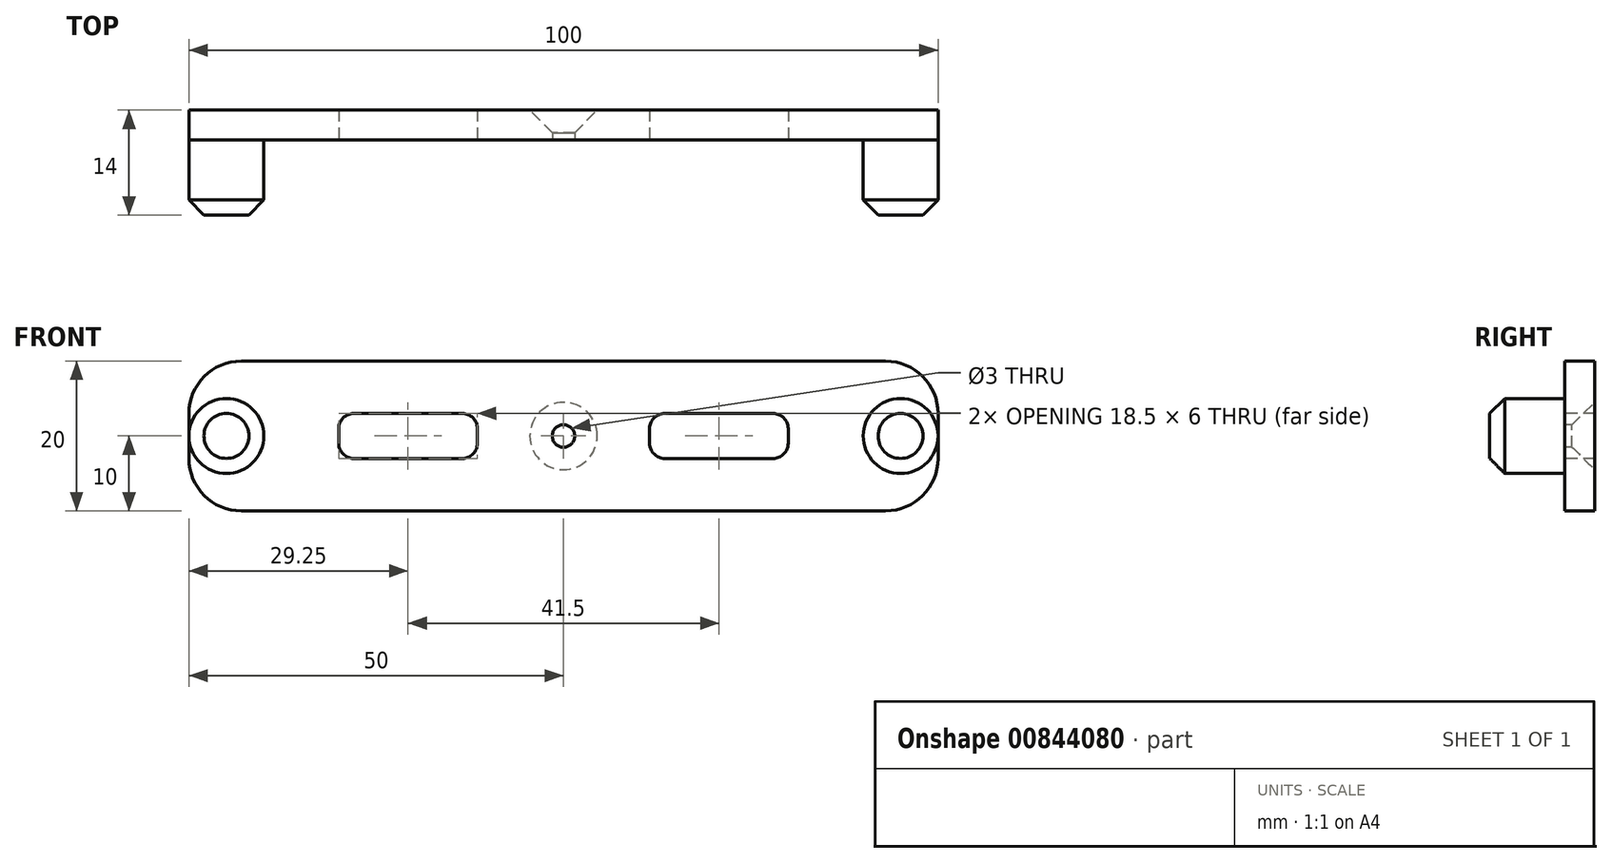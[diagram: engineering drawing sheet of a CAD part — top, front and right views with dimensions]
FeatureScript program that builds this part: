
annotation { "Feature Type Name" : "Feature", "Feature Type Description" : "" }
export const myFeature = defineFeature(function(context is Context, id is Id, definition is map)
    precondition{}
    {
        {
            var Q0;
            Q0=qCreatedBy(makeId("Front.planeOp"),FACE);
            var sketch = newSketch(context, id + "F0", { "sketchPlane" : qUnion([Q0])});
            skLineSegment(sketch, "E0.bottom", {"start": v(-50, 10) * mm, "end": v(50, 10) * mm});
            skLineSegment(sketch, "E0.top", {"start": v(-50, -10) * mm, "end": v(50, -10) * mm});
            skLineSegment(sketch, "E0.left", {"start": v(-50, 10) * mm, "end": v(-50, -10) * mm});
            skLineSegment(sketch, "E0.right", {"start": v(50, 10) * mm, "end": v(50, -10) * mm});
            skPoint(sketch, "E0.middle", {"position": v(0, 0) * mm});
            skSolve(sketch);
        }
        {
            var Q0;
            Q0=makeQuery(id+"F0.imprint","IMPRINT",FACE,{"disambiguationData":[TD([[makeQuery(id+"F0.imprint","IMPRINT",EDGE,{"derivedFrom":sQuery(id+"F0.wireOp",EDGE,"E0.bottom")}),-1.0]])]});
            extrude(context, id + "F1", {"entities" : qUnion([Q0]), "depth" : 4 * mm, "offsetDistance" : 25 * mm});
        }
        {
            var Q0;
            Q0=makeQuery(id+"F1.opExtrude","CAP_FACE",FACE,{"disambiguationData":[OSD([sQuery(id+"F0.wireOp",EDGE,"E0.bottom"),sQuery(id+"F0.wireOp",EDGE,"E0.top"),sQuery(id+"F0.wireOp",EDGE,"E0.left"),sQuery(id+"F0.wireOp",EDGE,"E0.right")])],"isStart":false});
            var sketch = newSketch(context, id + "F2", { "sketchPlane" : qUnion([Q0])});
            skCircle(sketch, "E1", {"center": v(-45, 0) * mm, "radius": 5 * mm});
            skPoint(sketch, "E1.centerSnap0", {"position": v(-50, 0) * mm});
            skCircle(sketch, "E2", {"center": v(45, 0) * mm, "radius": 5 * mm});
            skSolve(sketch);
        }
        {
            var Q0;
            Q0=makeQuery(id+"F2.imprint","IMPRINT",FACE,{"disambiguationData":[TD([[makeQuery(id+"F2.imprint","IMPRINT",EDGE,{"derivedFrom":sQuery(id+"F2.wireOp",EDGE,"E1")}),1.0]])]});
            var Q1;
            Q1=makeQuery(id+"F2.imprint","IMPRINT",FACE,{"disambiguationData":[TD([[makeQuery(id+"F2.imprint","IMPRINT",EDGE,{"derivedFrom":sQuery(id+"F2.wireOp",EDGE,"E2")}),1.0]])]});
            extrude(context, id + "F3", {"entities" : qUnion([Q0, Q1]), "operationType" : NewBodyOperationType.ADD, "depth" : 10 * mm, "offsetDistance" : 25 * mm});
        }
        {
            var Q0;
            Q0=makeQuery(id+"F1.opExtrude","SWEPT_EDGE",EDGE,{"disambiguationData":[OSD([sQuery(id+"F0.wireOp",EDGE,"E0.top"),sQuery(id+"F0.wireOp",EDGE,"E0.left")])]});
            var Q1;
            Q1=makeQuery(id+"F1.opExtrude","SWEPT_EDGE",EDGE,{"disambiguationData":[OSD([sQuery(id+"F0.wireOp",EDGE,"E0.top"),sQuery(id+"F0.wireOp",EDGE,"E0.right")])]});
            var Q2;
            Q2=makeQuery(id+"F1.opExtrude","SWEPT_EDGE",EDGE,{"disambiguationData":[OSD([sQuery(id+"F0.wireOp",EDGE,"E0.bottom"),sQuery(id+"F0.wireOp",EDGE,"E0.right")])]});
            var Q3;
            Q3=makeQuery(id+"F1.opExtrude","SWEPT_EDGE",EDGE,{"disambiguationData":[OSD([sQuery(id+"F0.wireOp",EDGE,"E0.bottom"),sQuery(id+"F0.wireOp",EDGE,"E0.left")])]});
            fillet(context, id + "F4", {"entities" : qUnion([Q0, Q1, Q2, Q3]), "radius" : 7 * mm, "tangentPropagation" : true, "allowEdgeOverflow" : false});
        }
        {
            var Q0;
            Q0=makeQuery(id+"F1.opExtrude","CAP_FACE",FACE,{"disambiguationData":[OSD([sQuery(id+"F0.wireOp",EDGE,"E0.bottom"),sQuery(id+"F0.wireOp",EDGE,"E0.top"),sQuery(id+"F0.wireOp",EDGE,"E0.left"),sQuery(id+"F0.wireOp",EDGE,"E0.right")])],"isStart":false});
            var sketch = newSketch(context, id + "F5", { "sketchPlane" : qUnion([Q0])});
            skCircle(sketch, "E3", {"center": v(0, 0) * mm, "radius": 1.5 * mm});
            skSolve(sketch);
        }
        {
            var Q0;
            Q0 = qSketchRegion(id + "F5", true);
            extrude(context, id + "F6", {"entities" : qUnion([Q0]), "operationType" : NewBodyOperationType.REMOVE, "oppositeDirection" : true, "depth" : 25 * mm, "offsetDistance" : 25 * mm});
        }
        {
            var Q0;
            Q0=makeQuery(id+"F6.boolean.opBoolean","INTERSECT",EDGE,{"derivedFrom":[makeQuery(id+"F1.opExtrude","CAP_FACE",FACE,{"disambiguationData":[OSD([sQuery(id+"F0.wireOp",EDGE,"E0.bottom"),sQuery(id+"F0.wireOp",EDGE,"E0.top"),sQuery(id+"F0.wireOp",EDGE,"E0.left"),sQuery(id+"F0.wireOp",EDGE,"E0.right")])],"isStart":true}),makeQuery(id+"F6.opExtrude","SWEPT_FACE",FACE,{"disambiguationData":[OSD([sQuery(id+"F5.wireOp",EDGE,"E3")])]})]});
            chamfer(context, id + "F7", {"entities" : qUnion([Q0]), "width" : 3 * mm, "tangentPropagation" : true});
        }
        {
            var Q0;
            Q0=makeQuery(id+"F1.opExtrude","CAP_FACE",FACE,{"disambiguationData":[OSD([sQuery(id+"F0.wireOp",EDGE,"E0.bottom"),sQuery(id+"F0.wireOp",EDGE,"E0.top"),sQuery(id+"F0.wireOp",EDGE,"E0.left"),sQuery(id+"F0.wireOp",EDGE,"E0.right")])],"isStart":false});
            var sketch = newSketch(context, id + "F8", { "sketchPlane" : qUnion([Q0])});
            skLineSegment(sketch, "E4.bottom", {"start": v(-30, 3) * mm, "end": v(-11.5, 3) * mm});
            skLineSegment(sketch, "E4.top", {"start": v(-30, -3) * mm, "end": v(-11.5, -3) * mm});
            skLineSegment(sketch, "E4.left", {"start": v(-30, 3) * mm, "end": v(-30, -3) * mm});
            skLineSegment(sketch, "E4.right", {"start": v(-11.5, 3) * mm, "end": v(-11.5, -3) * mm});
            skLineSegment(sketch, "E5", {"start": v(0, 0) * mm, "end": v(0, 30.26) * mm, "construction": true});
            skLineSegment(sketch, "E6.MirrorCS", {"start": v(30, 3) * mm, "end": v(11.5, 3) * mm});
            skLineSegment(sketch, "E7.MirrorCS", {"start": v(11.5, 3) * mm, "end": v(11.5, -3) * mm});
            skLineSegment(sketch, "E8.MirrorCS", {"start": v(30, 3) * mm, "end": v(30, -3) * mm});
            skLineSegment(sketch, "E9.MirrorCS", {"start": v(30, -3) * mm, "end": v(11.5, -3) * mm});
            skSolve(sketch);
        }
        {
            var Q0;
            Q0 = qSketchRegion(id + "F8", true);
            extrude(context, id + "F9", {"entities" : qUnion([Q0]), "operationType" : NewBodyOperationType.REMOVE, "oppositeDirection" : true, "depth" : 25 * mm, "offsetDistance" : 25 * mm});
        }
        {
            var Q0;
            Q0=makeQuery(id+"F9.boolean.opBoolean","COPY",EDGE,{"derivedFrom":makeQuery(id+"F9.opExtrude","SWEPT_EDGE",EDGE,{"disambiguationData":[OSD([sQuery(id+"F8.wireOp",EDGE,"E4.bottom"),sQuery(id+"F8.wireOp",EDGE,"E4.left")])]})});
            var Q1;
            Q1=makeQuery(id+"F9.boolean.opBoolean","COPY",EDGE,{"derivedFrom":makeQuery(id+"F9.opExtrude","SWEPT_EDGE",EDGE,{"disambiguationData":[OSD([sQuery(id+"F8.wireOp",EDGE,"E4.top"),sQuery(id+"F8.wireOp",EDGE,"E4.left")])]})});
            var Q2;
            Q2=makeQuery(id+"F9.boolean.opBoolean","COPY",EDGE,{"derivedFrom":makeQuery(id+"F9.opExtrude","SWEPT_EDGE",EDGE,{"disambiguationData":[OSD([sQuery(id+"F8.wireOp",EDGE,"E4.bottom"),sQuery(id+"F8.wireOp",EDGE,"E4.right")])]})});
            var Q3;
            Q3=makeQuery(id+"F9.boolean.opBoolean","COPY",EDGE,{"derivedFrom":makeQuery(id+"F9.opExtrude","SWEPT_EDGE",EDGE,{"disambiguationData":[OSD([sQuery(id+"F8.wireOp",EDGE,"E4.top"),sQuery(id+"F8.wireOp",EDGE,"E4.right")])]})});
            var Q4;
            Q4=makeQuery(id+"F9.boolean.opBoolean","COPY",EDGE,{"derivedFrom":makeQuery(id+"F9.opExtrude","SWEPT_EDGE",EDGE,{"disambiguationData":[OSD([sQuery(id+"F8.wireOp",EDGE,"E8.MirrorCS"),sQuery(id+"F8.wireOp",EDGE,"E9.MirrorCS")])]})});
            var Q5;
            Q5=makeQuery(id+"F9.boolean.opBoolean","COPY",EDGE,{"derivedFrom":makeQuery(id+"F9.opExtrude","SWEPT_EDGE",EDGE,{"disambiguationData":[OSD([sQuery(id+"F8.wireOp",EDGE,"E7.MirrorCS"),sQuery(id+"F8.wireOp",EDGE,"E9.MirrorCS")])]})});
            var Q6;
            Q6=makeQuery(id+"F9.boolean.opBoolean","COPY",EDGE,{"derivedFrom":makeQuery(id+"F9.opExtrude","SWEPT_EDGE",EDGE,{"disambiguationData":[OSD([sQuery(id+"F8.wireOp",EDGE,"E6.MirrorCS"),sQuery(id+"F8.wireOp",EDGE,"E7.MirrorCS")])]})});
            var Q7;
            Q7=makeQuery(id+"F9.boolean.opBoolean","COPY",EDGE,{"derivedFrom":makeQuery(id+"F9.opExtrude","SWEPT_EDGE",EDGE,{"disambiguationData":[OSD([sQuery(id+"F8.wireOp",EDGE,"E6.MirrorCS"),sQuery(id+"F8.wireOp",EDGE,"E8.MirrorCS")])]})});
            fillet(context, id + "F10", {"entities" : qUnion([Q0, Q1, Q2, Q3, Q4, Q5, Q6, Q7]), "radius" : 2 * mm, "tangentPropagation" : true, "allowEdgeOverflow" : false});
        }
        {
            var Q0;
            Q0=makeQuery(id+"F3.opExtrude","CAP_EDGE",EDGE,{"disambiguationData":[OSD([sQuery(id+"F2.wireOp",EDGE,"E1")])],"isStart":false});
            var Q1;
            Q1=makeQuery(id+"F3.opExtrude","CAP_EDGE",EDGE,{"disambiguationData":[OSD([sQuery(id+"F2.wireOp",EDGE,"E2")])],"isStart":false});
            chamfer(context, id + "F11", {"entities" : qUnion([Q0, Q1]), "width" : 2 * mm, "tangentPropagation" : true});
        }
    });
